# Revit family: Karlsson_Pictogram_Rainbow_Black_Clock_14318
name_source: partatom
category: Generic Models
units: mm (PartAtom-declared; Revit-internal decimal feet)

## family parameters
Can host rebar = No
Cut with Voids When Loaded = No
Host = Face
Part Type = Normal
Room Calculation Point = No
Round Connector Dimension = Use Diameter
Shared = No

## types (1)
- Karlsson_Pictogram_Rainbow_Black_Clock_14318
    Cost = 27.3 $
    Default Elevation = 4' - 0"
    Description = Dramatically simple, the stunning Pictogram Rainbow Wall Clock adds a dash of instant, vibrant modern colour to any monotone contemporary room colour scheme. The classic circular steel clock has an attractive black face, bold white hands and beautiful colour coded hour markings. The visually striking timepiece is ideal for wall mounting in a kitchen, home office or stylish living room.
    Manufacturer = Karlsson
    Model = Pictogram Rainbow Wall Clock, Black
    URL = http://mydeco.com

## geometry (parser evidence)
native form markers: Sweep x3
no freeform markers — native parametric forms only
